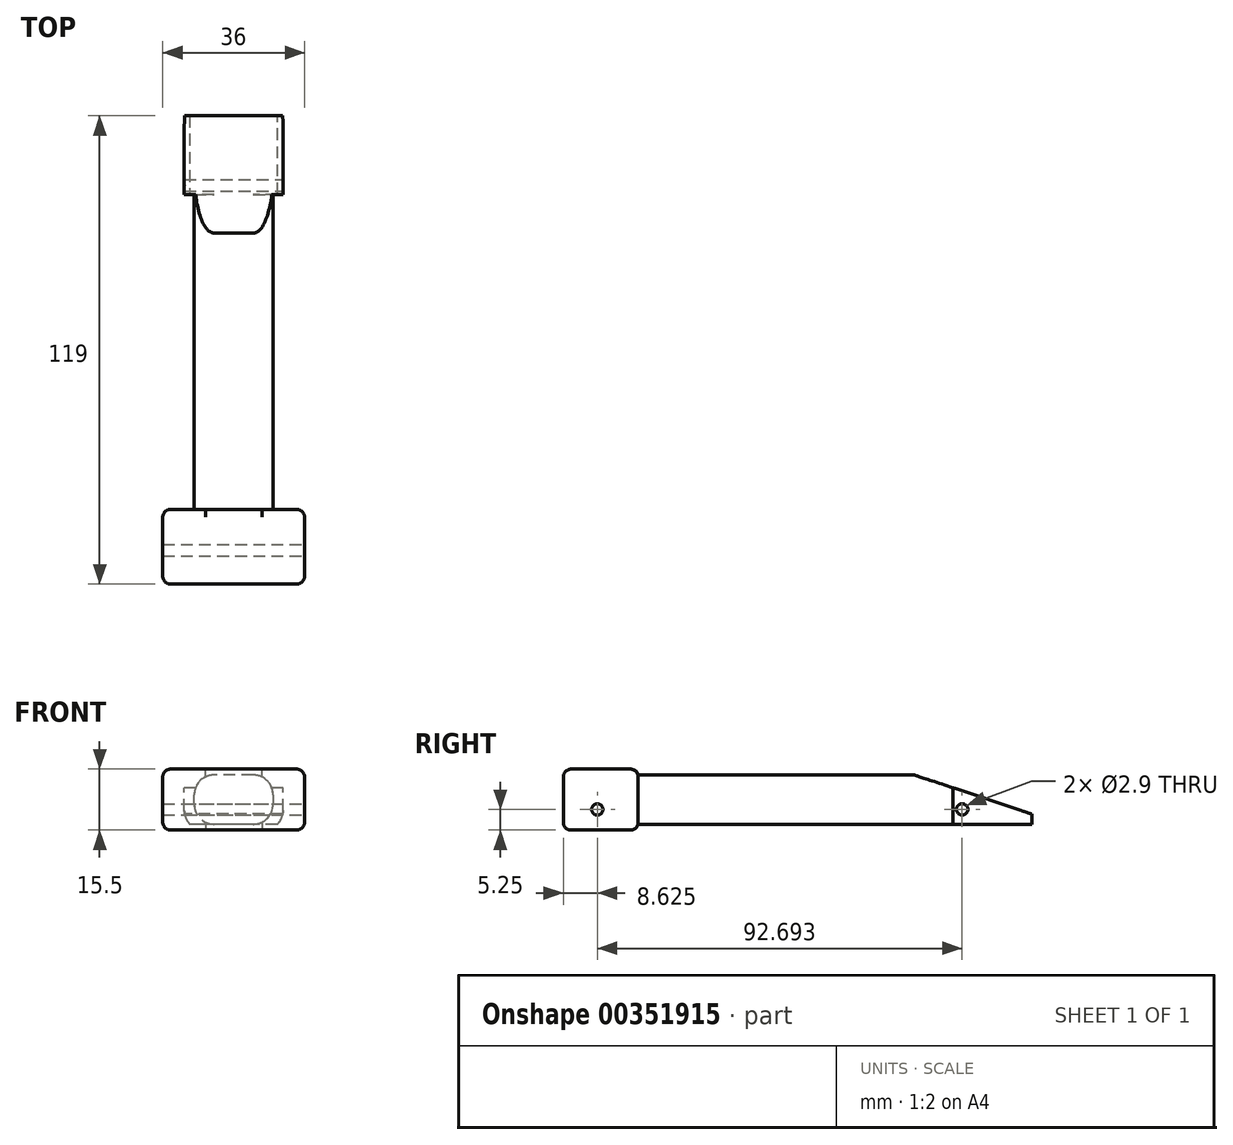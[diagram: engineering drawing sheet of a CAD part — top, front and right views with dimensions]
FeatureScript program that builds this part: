
annotation { "Feature Type Name" : "Feature", "Feature Type Description" : "" }
export const myFeature = defineFeature(function(context is Context, id is Id, definition is map)
    precondition{}
    {
        {
            var Q0;
            Q0=qCreatedBy(makeId("Right.planeOp"),FACE);
            var sketch = newSketch(context, id + "F0", { "sketchPlane" : qUnion([Q0])});
            skLineSegment(sketch, "E0", {"start": v(0, 0) * mm, "end": v(0, 12.5) * mm});
            skLineSegment(sketch, "E1", {"start": v(0, 12.5) * mm, "end": v(-80, 12.5) * mm});
            skLineSegment(sketch, "E2", {"start": v(-80, 12.5) * mm, "end": v(-80, 0) * mm});
            skLineSegment(sketch, "E3", {"start": v(-80, 0) * mm, "end": v(0, 0) * mm});
            skSolve(sketch);
        }
        {
            var Q0;
            Q0 = qSketchRegion(id + "F0", true);
            extrude(context, id + "F1", {"entities" : qUnion([Q0]), "depth" : 20 * mm});
        }
        {
            var Q0;
            Q0=makeQuery(id+"F1.opExtrude","CAP_EDGE",EDGE,{"disambiguationData":[OSD([sQuery(id+"F0.wireOp",EDGE,"E1")])],"isStart":false});
            var Q1;
            Q1=makeQuery(id+"F1.opExtrude","CAP_EDGE",EDGE,{"disambiguationData":[OSD([sQuery(id+"F0.wireOp",EDGE,"E3")])],"isStart":false});
            var Q2;
            Q2=makeQuery(id+"F1.opExtrude","CAP_EDGE",EDGE,{"disambiguationData":[OSD([sQuery(id+"F0.wireOp",EDGE,"E1")])],"isStart":true});
            var Q3;
            Q3=makeQuery(id+"F1.opExtrude","CAP_EDGE",EDGE,{"disambiguationData":[OSD([sQuery(id+"F0.wireOp",EDGE,"E3")])],"isStart":true});
            fillet(context, id + "F2", {"entities" : qUnion([Q0, Q1, Q2, Q3]), "radius" : 5 * mm, "tangentPropagation" : true, "allowEdgeOverflow" : false});
        }
        {
            var Q0;
            Q0=makeQuery(id+"F1.opExtrude","SWEPT_FACE",FACE,{"disambiguationData":[OSD([sQuery(id+"F0.wireOp",EDGE,"E0")])]});
            var sketch = newSketch(context, id + "F3", { "sketchPlane" : qUnion([Q0])});
            skLineSegment(sketch, "E4", {"start": v(-22.54, 11.04) * mm, "end": v(-22.54, 14.04) * mm});
            skLineSegment(sketch, "E5", {"start": v(2.54, 11.04) * mm, "end": v(2.54, 14.04) * mm});
            skLineSegment(sketch, "E6", {"start": v(2.54, 14.04) * mm, "end": v(-22.54, 14.04) * mm});
            skLineSegment(sketch, "E7", {"start": v(-18.54, -1.54) * mm, "end": v(2.54, -1.54) * mm});
            skLineSegment(sketch, "E8", {"start": v(2.54, -1.54) * mm, "end": v(2.54, 11.04) * mm});
            skLineSegment(sketch, "E9", {"start": v(-22.54, 11.04) * mm, "end": v(-22.54, -1.54) * mm});
            skLineSegment(sketch, "E10", {"start": v(-22.54, -1.54) * mm, "end": v(-18.54, -1.54) * mm});
            skPoint(sketch, "E11.start.orphan", {"position": v(-18.54, 11.04) * mm});
            skPoint(sketch, "E12.start.orphan", {"position": v(-1.46, 11.04) * mm});
            skPoint(sketch, "E13.start.orphan", {"position": v(-1.46, 1.46) * mm});
            skPoint(sketch, "E14.start.orphan", {"position": v(-18.54, 1.46) * mm});
            skSolve(sketch);
        }
        {
            var Q0;
            Q0 = qSketchRegion(id + "F3", true);
            extrude(context, id + "F4", {"entities" : qUnion([Q0]), "operationType" : NewBodyOperationType.ADD, "depth" : 20 * mm});
        }
        {
            var Q0;
            Q0=makeQuery(id+"F4.opExtrude","SWEPT_EDGE",EDGE,{"disambiguationData":[OSD([sQuery(id+"F3.wireOp",EDGE,"E4"),sQuery(id+"F3.wireOp",EDGE,"E6")])]});
            var Q1;
            Q1=makeQuery(id+"F4.opExtrude","SWEPT_EDGE",EDGE,{"disambiguationData":[OSD([sQuery(id+"F3.wireOp",EDGE,"E9"),sQuery(id+"F3.wireOp",EDGE,"E10")])]});
            var Q2;
            Q2=makeQuery(id+"F4.opExtrude","SWEPT_EDGE",EDGE,{"disambiguationData":[OSD([sQuery(id+"F3.wireOp",EDGE,"E7"),sQuery(id+"F3.wireOp",EDGE,"E8")])]});
            var Q3;
            Q3=makeQuery(id+"F4.opExtrude","SWEPT_EDGE",EDGE,{"disambiguationData":[OSD([sQuery(id+"F3.wireOp",EDGE,"E5"),sQuery(id+"F3.wireOp",EDGE,"E6")])]});
            fillet(context, id + "F5", {"entities" : qUnion([Q0, Q1, Q2, Q3]), "radius" : 5 * mm, "tangentPropagation" : true, "allowEdgeOverflow" : false});
        }
        {
            var Q0;
            Q0=qCreatedBy(makeId("Right.planeOp"),FACE);
            var sketch = newSketch(context, id + "F6", { "sketchPlane" : qUnion([Q0])});
            skLineSegment(sketch, "E15", {"start": v(0, 0) * mm, "end": v(20, 0) * mm});
            skPoint(sketch, "E15.startSnap0", {"position": v(20, 0.96) * mm});
            skLineSegment(sketch, "E16", {"start": v(20, 0) * mm, "end": v(20, 2.57) * mm});
            skLineSegment(sketch, "E17", {"start": v(20, 2.57) * mm, "end": v(-9.84, 12.5) * mm});
            skLineSegment(sketch, "E18", {"start": v(0, 0) * mm, "end": v(0, -2.49) * mm});
            skLineSegment(sketch, "E19", {"start": v(0, -2.49) * mm, "end": v(20, -2.49) * mm});
            skLineSegment(sketch, "E20", {"start": v(20, 14.38) * mm, "end": v(-15.48, 14.38) * mm});
            skLineSegment(sketch, "E21", {"start": v(-9.84, 12.5) * mm, "end": v(-15.48, 14.38) * mm});
            skLineSegment(sketch, "E22", {"start": v(20, -2.49) * mm, "end": v(23.49, -2.49) * mm});
            skLineSegment(sketch, "E23", {"start": v(20, 14.38) * mm, "end": v(23.45, 14.38) * mm});
            skLineSegment(sketch, "E24", {"start": v(23.45, 14.38) * mm, "end": v(23.49, -2.49) * mm});
            skSolve(sketch);
        }
        {
            var Q0;
            Q0 = qSketchRegion(id + "F6", true);
            extrude(context, id + "F7", {"entities" : qUnion([Q0]), "operationType" : NewBodyOperationType.REMOVE, "depth" : 25 * mm});
        }
        {
            var Q0;
            {var subQ4=sQuery(id+"F3.wireOp",EDGE,"E6");var subQ5=sQuery(id+"F3.wireOp",EDGE,"E5");var subQ7=sQuery(id+"F6.wireOp",EDGE,"E21");var subQ8=sQuery(id+"F6.wireOp",EDGE,"E17");Q0=makeQuery(id+"F7.boolean.opBoolean","COPY",FACE,{"disambiguationData":[TD([makeQuery(id+"F5.opFillet","BLEND_FACE",FACE,{"disambiguationData":[OSD([subQ5,subQ4])]})])],"derivedFrom":makeQuery(id+"F7.opExtrude","CAP_FACE",FACE,{"disambiguationData":[OSD([sQuery(id+"F6.wireOp",EDGE,"E15"),subQ8,sQuery(id+"F6.wireOp",EDGE,"E18"),sQuery(id+"F6.wireOp",EDGE,"E19"),sQuery(id+"F6.wireOp",EDGE,"E16"),sQuery(id+"F6.wireOp",EDGE,"E20"),subQ7,sQuery(id+"F6.wireOp",EDGE,"E22"),sQuery(id+"F6.wireOp",EDGE,"E23"),sQuery(id+"F6.wireOp",EDGE,"E24")])],"isStart":true})});}
            var sketch = newSketch(context, id + "F8", { "sketchPlane" : qUnion([Q0])});
            skLineSegment(sketch, "E25", {"start": v(20, 2.57) * mm, "end": v(0, 9.23) * mm});
            skLineSegment(sketch, "E26", {"start": v(0, 9.23) * mm, "end": v(0, 13.39) * mm});
            skLineSegment(sketch, "E27", {"start": v(0, 13.39) * mm, "end": v(20, 13.39) * mm});
            skLineSegment(sketch, "E28", {"start": v(20, 13.39) * mm, "end": v(20, 2.57) * mm});
            skSolve(sketch);
        }
        {
            var Q0;
            Q0 = qSketchRegion(id + "F8", true);
            extrude(context, id + "F9", {"entities" : qUnion([Q0]), "operationType" : NewBodyOperationType.REMOVE, "oppositeDirection" : true, "depth" : 25 * mm});
        }
        {
            var Q0;
            {var subQ7=sQuery(id+"F6.wireOp",EDGE,"E15");Q0=makeQuery(id+"F7.boolean.opBoolean","COPY",FACE,{"disambiguationData":[TD([makeQuery(id+"F1.opExtrude","SWEPT_FACE",FACE,{"disambiguationData":[OSD([sQuery(id+"F0.wireOp",EDGE,"E3")])]})])],"derivedFrom":makeQuery(id+"F7.opExtrude","CAP_FACE",FACE,{"disambiguationData":[OSD([subQ7,sQuery(id+"F6.wireOp",EDGE,"E17"),sQuery(id+"F6.wireOp",EDGE,"E18"),sQuery(id+"F6.wireOp",EDGE,"E19"),sQuery(id+"F6.wireOp",EDGE,"E16"),sQuery(id+"F6.wireOp",EDGE,"E20"),sQuery(id+"F6.wireOp",EDGE,"E21"),sQuery(id+"F6.wireOp",EDGE,"E22"),sQuery(id+"F6.wireOp",EDGE,"E23"),sQuery(id+"F6.wireOp",EDGE,"E24")])],"isStart":true})});}
            var sketch = newSketch(context, id + "F10", { "sketchPlane" : qUnion([Q0])});
            skLineSegment(sketch, "E29", {"start": v(0, -0.89) * mm, "end": v(20, -0.89) * mm});
            skLineSegment(sketch, "E30", {"start": v(20, -0.89) * mm, "end": v(20, 0) * mm});
            skLineSegment(sketch, "E31", {"start": v(20, 0) * mm, "end": v(0, 0) * mm});
            skLineSegment(sketch, "E32", {"start": v(0, 0) * mm, "end": v(0, -0.89) * mm});
            skSolve(sketch);
        }
        {
            var Q0;
            Q0 = qSketchRegion(id + "F10", true);
            extrude(context, id + "F11", {"entities" : qUnion([Q0]), "operationType" : NewBodyOperationType.REMOVE, "oppositeDirection" : true, "depth" : 25 * mm});
        }
        {
            var Q0;
            Q0=makeQuery(id+"F1.opExtrude","SWEPT_FACE",FACE,{"disambiguationData":[OSD([sQuery(id+"F0.wireOp",EDGE,"E2")])]});
            var sketch = newSketch(context, id + "F12", { "sketchPlane" : qUnion([Q0])});
            skLineSegment(sketch, "E33", {"start": v(-8, 0) * mm, "end": v(-8, 12.5) * mm});
            skLineSegment(sketch, "E34", {"start": v(28, 0) * mm, "end": v(28, 14) * mm});
            skLineSegment(sketch, "E35", {"start": v(-8, 0) * mm, "end": v(-8, -1.5) * mm});
            skLineSegment(sketch, "E36", {"start": v(-8, -1.5) * mm, "end": v(28, -1.5) * mm});
            skLineSegment(sketch, "E37", {"start": v(28, 0) * mm, "end": v(28, -1.5) * mm});
            skPoint(sketch, "E38.start.orphan", {"position": v(-8, 14) * mm});
            skLineSegment(sketch, "E39", {"start": v(-8, 12.5) * mm, "end": v(-8, 14) * mm});
            skLineSegment(sketch, "E40", {"start": v(-8, 14) * mm, "end": v(28, 14) * mm});
            skPoint(sketch, "E41.end.orphan", {"position": v(20, 0) * mm});
            skSolve(sketch);
        }
        {
            var Q0;
            Q0 = qSketchRegion(id + "F12", true);
            extrude(context, id + "F13", {"entities" : qUnion([Q0]), "operationType" : NewBodyOperationType.ADD, "depth" : 19 * mm});
        }
        {
            var Q0;
            Q0=makeQuery(id+"F13.opExtrude","CAP_EDGE",EDGE,{"disambiguationData":[OSD([sQuery(id+"F12.wireOp",EDGE,"E33"),sQuery(id+"F12.wireOp",EDGE,"E35"),sQuery(id+"F12.wireOp",EDGE,"E39")])],"isStart":true});
            var Q1;
            Q1=makeQuery(id+"F13.opExtrude","SWEPT_FACE",FACE,{"disambiguationData":[OSD([sQuery(id+"F12.wireOp",EDGE,"E40")])]});
            var Q2;
            Q2=makeQuery(id+"F13.opExtrude","SWEPT_FACE",FACE,{"disambiguationData":[OSD([sQuery(id+"F12.wireOp",EDGE,"E34"),sQuery(id+"F12.wireOp",EDGE,"E37")])]});
            var Q3;
            Q3=makeQuery(id+"F13.opExtrude","SWEPT_FACE",FACE,{"disambiguationData":[OSD([sQuery(id+"F12.wireOp",EDGE,"E36")])]});
            var Q4;
            Q4=makeQuery(id+"F13.opExtrude","SWEPT_FACE",FACE,{"disambiguationData":[OSD([sQuery(id+"F12.wireOp",EDGE,"E33"),sQuery(id+"F12.wireOp",EDGE,"E35"),sQuery(id+"F12.wireOp",EDGE,"E39")])]});
            fillet(context, id + "F14", {"entities" : qUnion([Q0, Q1, Q2, Q3, Q4]), "radius" : 2 * mm, "tangentPropagation" : true, "allowEdgeOverflow" : false});
        }
        {
            var Q0;
            Q0=makeQuery(id+"F13.opExtrude","SWEPT_FACE",FACE,{"disambiguationData":[OSD([sQuery(id+"F12.wireOp",EDGE,"E34"),sQuery(id+"F12.wireOp",EDGE,"E37")])]});
            var sketch = newSketch(context, id + "F15", { "sketchPlane" : qUnion([Q0])});
            skCircle(sketch, "E42", {"center": v(-90.37, 3.75) * mm, "radius": 1.45 * mm});
            skCircle(sketch, "E43", {"center": v(2.32, 3.75) * mm, "radius": 1.45 * mm});
            skSolve(sketch);
        }
        {
            var Q0;
            Q0 = qSketchRegion(id + "F15", true);
            extrude(context, id + "F16", {"entities" : qUnion([Q0]), "operationType" : NewBodyOperationType.REMOVE, "oppositeDirection" : true, "depth" : 100 * mm});
        }
    });
